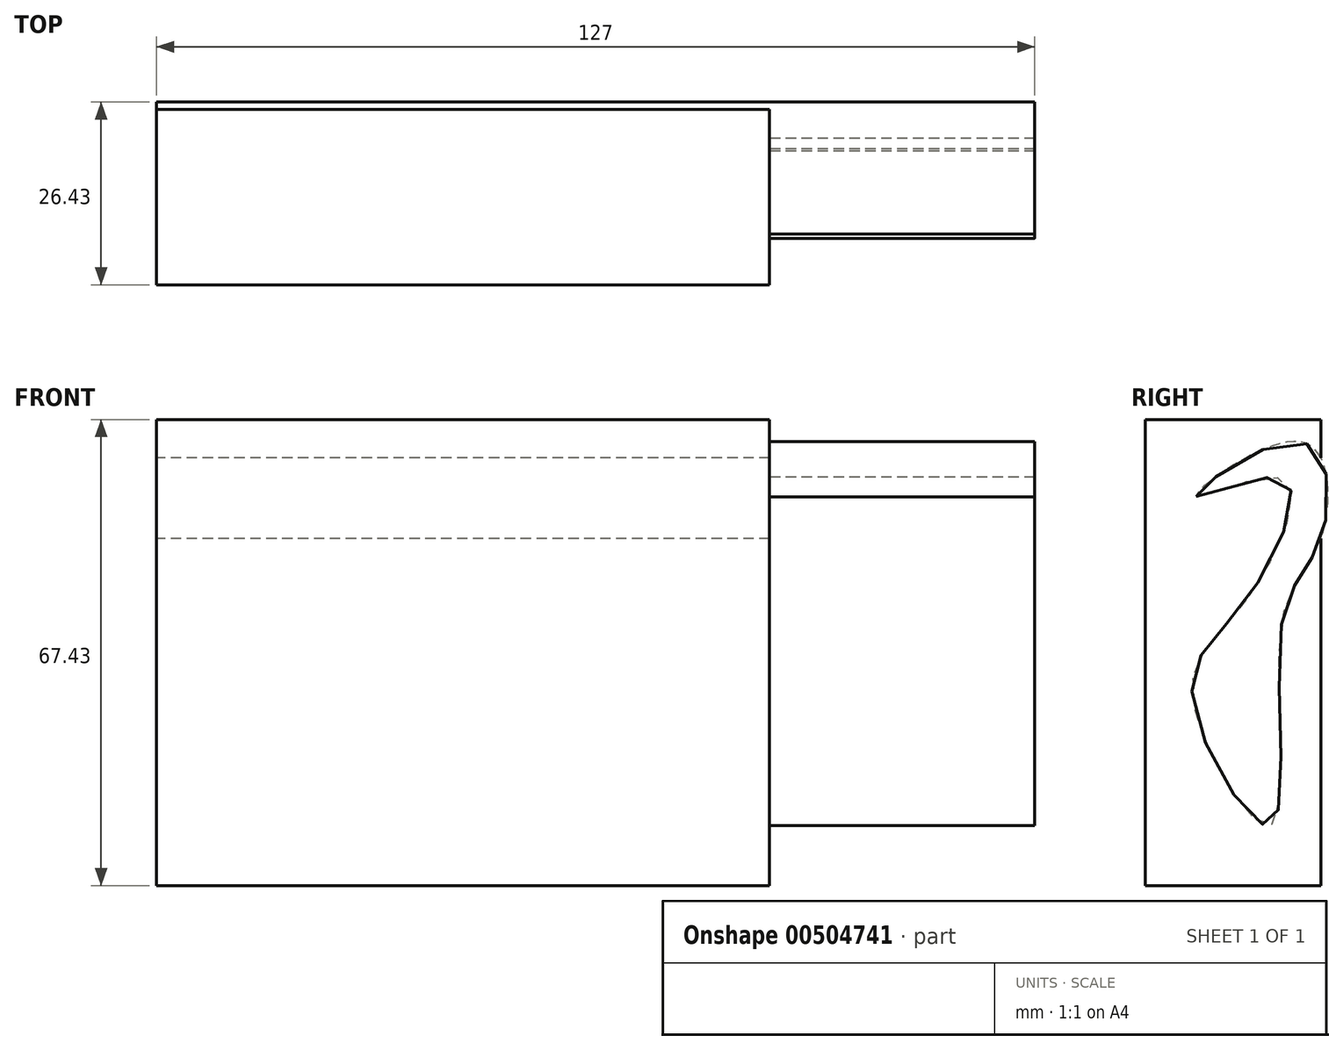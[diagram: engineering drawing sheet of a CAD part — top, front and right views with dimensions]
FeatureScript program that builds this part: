
annotation { "Feature Type Name" : "Feature", "Feature Type Description" : "" }
export const myFeature = defineFeature(function(context is Context, id is Id, definition is map)
    precondition{}
    {
        {
            var Q0;
            Q0=qCreatedBy(makeId("Front.planeOp"),FACE);
            var sketch = newSketch(context, id + "F0", { "sketchPlane" : qUnion([Q0])});
            skLineSegment(sketch, "E0", {"start": v(-53.67, 51.5) * mm, "end": v(-53.67, -15.92) * mm});
            skLineSegment(sketch, "E1", {"start": v(-53.67, -15.92) * mm, "end": v(35, -15.92) * mm});
            skLineSegment(sketch, "E2", {"start": v(35, -15.92) * mm, "end": v(35, 51.5) * mm});
            skLineSegment(sketch, "E3", {"start": v(35, 51.5) * mm, "end": v(-53.67, 51.5) * mm});
            skSolve(sketch);
        }
        {
            var Q0;
            Q0=makeQuery(id+"F0.imprint","IMPRINT",FACE,{"disambiguationData":[TD([[makeQuery(id+"F0.imprint","IMPRINT",EDGE,{"derivedFrom":sQuery(id+"F0.wireOp",EDGE,"E0")}),1.0]])]});
            extrude(context, id + "F1", {"entities" : qUnion([Q0]), "depth" : 25.4 * mm});
        }
        {
            var Q0;
            Q0=makeQuery(id+"F1.opExtrude","SWEPT_FACE",FACE,{"disambiguationData":[OSD([sQuery(id+"F0.wireOp",EDGE,"E0")])]});
            var sketch = newSketch(context, id + "F2", { "sketchPlane" : qUnion([Q0])});
            skFitSpline(sketch, "E4", {"points": [v(18, 40.4) * mm, v(5.62, 42.95) * mm, v(10.93, 25.26) * mm, v(18.6, 11.3) * mm, v(7.4, -7.18) * mm, v(5.62, 22.31) * mm, v(0, 34.3) * mm, v(2.87, 48.26) * mm, v(18, 40.4) * mm]});
            skSolve(sketch);
        }
        {
            var Q0;
            Q0 = qSketchRegion(id + "F2", true);
            extrude(context, id + "F3", {"entities" : qUnion([Q0]), "operationType" : NewBodyOperationType.ADD, "depth" : -127 * mm});
        }
    });
